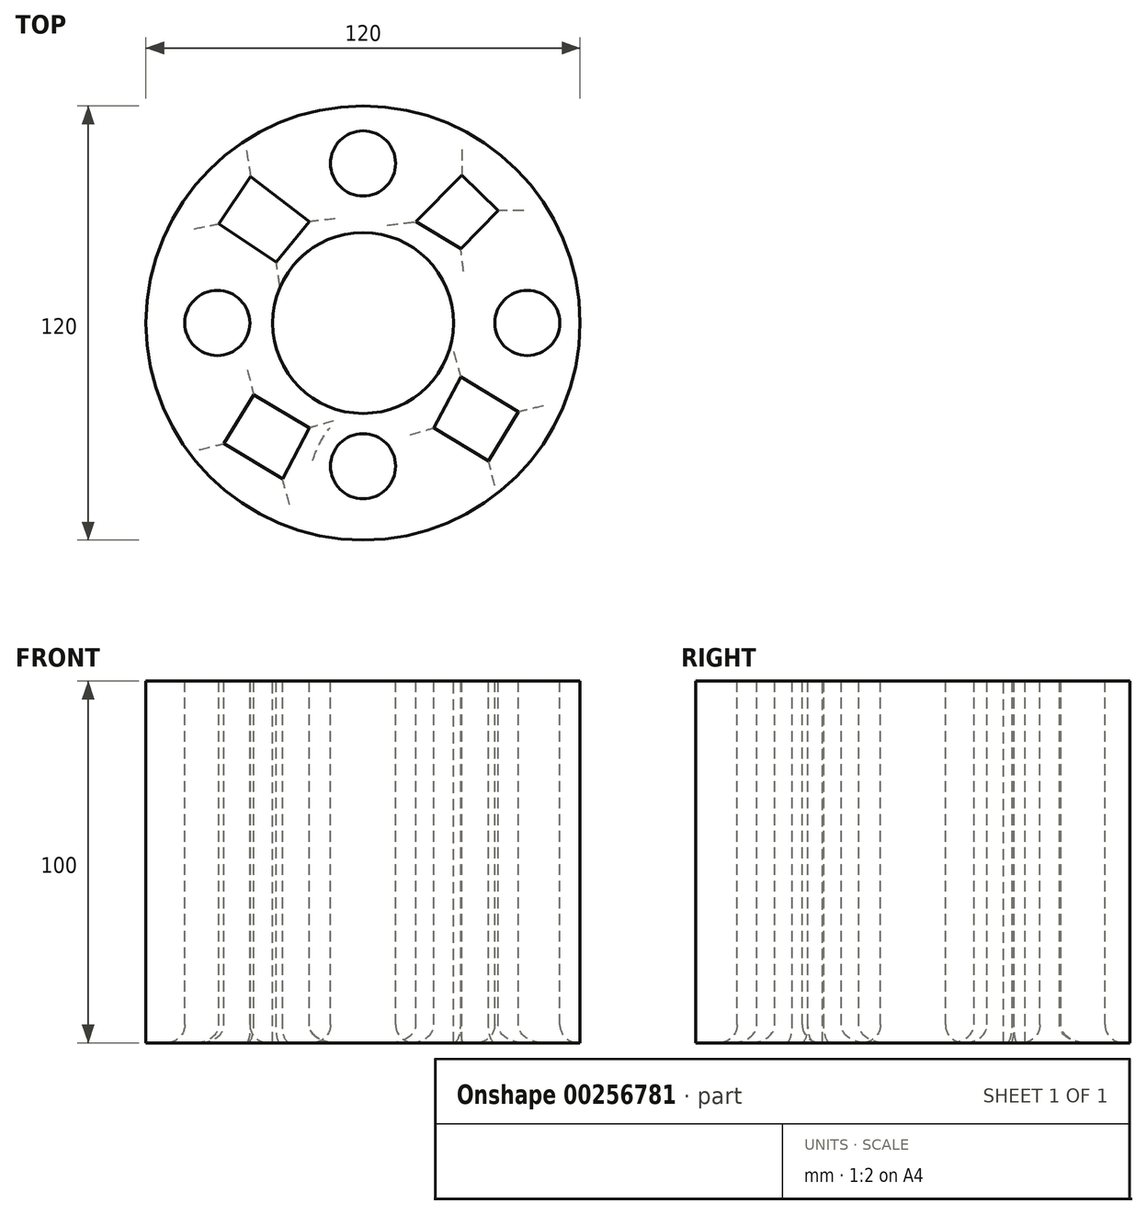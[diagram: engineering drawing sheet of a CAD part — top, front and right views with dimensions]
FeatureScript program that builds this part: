
annotation { "Feature Type Name" : "Feature", "Feature Type Description" : "" }
export const myFeature = defineFeature(function(context is Context, id is Id, definition is map)
    precondition{}
    {
        {
            var Q0;
            Q0=qCreatedBy(makeId("Top.planeOp"),FACE);
            var sketch = newSketch(context, id + "F0", { "sketchPlane" : qUnion([Q0])});
            skCircle(sketch, "E0", {"center": v(0, 0) * mm, "radius": 60 * mm});
            skSolve(sketch);
        }
        {
            var Q0;
            Q0 = qSketchRegion(id + "F0", true);
            extrude(context, id + "F1", {"entities" : qUnion([Q0]), "depth" : 100 * mm});
        }
        {
            var Q0;
            Q0=makeQuery(id+"F1.opExtrude","CAP_FACE",FACE,{"disambiguationData":[OSD([sQuery(id+"F0.wireOp",EDGE,"E0")])],"isStart":false});
            var sketch = newSketch(context, id + "F2", { "sketchPlane" : qUnion([Q0])});
            skCircle(sketch, "E1", {"center": v(0, 0) * mm, "radius": 25 * mm});
            skSolve(sketch);
        }
        {
            var Q0;
            Q0 = qSketchRegion(id + "F2", true);
            extrude(context, id + "F3", {"entities" : qUnion([Q0]), "operationType" : NewBodyOperationType.REMOVE, "endBound" : BoundingType.THROUGH_ALL, "oppositeDirection" : true, "depth" : 25 * mm});
        }
        {
            var Q0;
            Q0=makeQuery(id+"F1.opExtrude","CAP_FACE",FACE,{"disambiguationData":[OSD([sQuery(id+"F0.wireOp",EDGE,"E0")])],"isStart":false});
            var sketch = newSketch(context, id + "F4", { "sketchPlane" : qUnion([Q0])});
            skCircle(sketch, "E2", {"center": v(0, 44.11) * mm, "radius": 9 * mm});
            skCircle(sketch, "E3", {"center": v(-40.28, 0) * mm, "radius": 9 * mm});
            skCircle(sketch, "E4", {"center": v(45.39, 0) * mm, "radius": 9 * mm});
            skCircle(sketch, "E5", {"center": v(0, -39.6) * mm, "radius": 9 * mm});
            skSolve(sketch);
        }
        {
            var Q0;
            Q0 = qSketchRegion(id + "F4", true);
            extrude(context, id + "F5", {"entities" : qUnion([Q0]), "operationType" : NewBodyOperationType.REMOVE, "endBound" : BoundingType.THROUGH_ALL, "oppositeDirection" : true, "depth" : 25 * mm});
        }
        {
            var Q0;
            Q0=makeQuery(id+"F1.opExtrude","CAP_FACE",FACE,{"disambiguationData":[OSD([sQuery(id+"F0.wireOp",EDGE,"E0")])],"isStart":false});
            var sketch = newSketch(context, id + "F6", { "sketchPlane" : qUnion([Q0])});
            skLineSegment(sketch, "E6", {"start": v(-14.83, 28) * mm, "end": v(-24, 16.88) * mm});
            skLineSegment(sketch, "E7", {"start": v(-24, 16.88) * mm, "end": v(-39.81, 27.42) * mm});
            skLineSegment(sketch, "E8", {"start": v(-39.81, 27.42) * mm, "end": v(-31.08, 40.53) * mm});
            skLineSegment(sketch, "E9", {"start": v(-31.08, 40.53) * mm, "end": v(-14.83, 28) * mm});
            skLineSegment(sketch, "E10", {"start": v(14.64, 28) * mm, "end": v(27.32, 40.89) * mm});
            skLineSegment(sketch, "E11", {"start": v(27.32, 40.89) * mm, "end": v(37.35, 31.01) * mm});
            skLineSegment(sketch, "E12", {"start": v(37.35, 31.01) * mm, "end": v(27, 20.51) * mm});
            skLineSegment(sketch, "E13", {"start": v(27, 20.51) * mm, "end": v(14.64, 28) * mm});
            skLineSegment(sketch, "E14", {"start": v(27, -14.93) * mm, "end": v(42.95, -24.6) * mm});
            skLineSegment(sketch, "E15", {"start": v(42.95, -24.6) * mm, "end": v(34.72, -38.18) * mm});
            skLineSegment(sketch, "E16", {"start": v(34.72, -38.18) * mm, "end": v(19.58, -29) * mm});
            skLineSegment(sketch, "E17", {"start": v(19.58, -29) * mm, "end": v(27, -14.93) * mm});
            skLineSegment(sketch, "E18", {"start": v(-14.83, -29) * mm, "end": v(-22.28, -43.12) * mm});
            skLineSegment(sketch, "E19", {"start": v(-22.28, -43.12) * mm, "end": v(-38.42, -33.34) * mm});
            skLineSegment(sketch, "E20", {"start": v(-38.42, -33.34) * mm, "end": v(-30.24, -19.85) * mm});
            skLineSegment(sketch, "E21", {"start": v(-30.24, -19.85) * mm, "end": v(-14.83, -29) * mm});
            skSolve(sketch);
        }
        {
            var Q0;
            Q0 = qSketchRegion(id + "F6", true);
            extrude(context, id + "F7", {"entities" : qUnion([Q0]), "operationType" : NewBodyOperationType.REMOVE, "endBound" : BoundingType.THROUGH_ALL, "oppositeDirection" : true, "depth" : 25 * mm});
        }
        {
            var Q0;
            Q0=makeQuery(id+"F7.boolean.opBoolean","COPY",EDGE,{"derivedFrom":makeQuery(id+"F7.opExtrude","CAP_EDGE",EDGE,{"disambiguationData":[OSD([sQuery(id+"F6.wireOp",EDGE,"E13")])],"isStart":true})});
            var Q1;
            Q1=makeQuery(id+"F7.boolean.opBoolean","INTERSECT",EDGE,{"derivedFrom":[makeQuery(id+"F1.opExtrude","CAP_FACE",FACE,{"disambiguationData":[OSD([sQuery(id+"F0.wireOp",EDGE,"E0")])],"isStart":true}),makeQuery(id+"F7.opExtrude","SWEPT_FACE",FACE,{"disambiguationData":[OSD([sQuery(id+"F6.wireOp",EDGE,"E13")])]})]});
            var Q2;
            Q2=makeQuery(id+"F7.boolean.opBoolean","INTERSECT",EDGE,{"derivedFrom":[makeQuery(id+"F1.opExtrude","CAP_FACE",FACE,{"disambiguationData":[OSD([sQuery(id+"F0.wireOp",EDGE,"E0")])],"isStart":true}),makeQuery(id+"F7.opExtrude","SWEPT_FACE",FACE,{"disambiguationData":[OSD([sQuery(id+"F6.wireOp",EDGE,"E10")])]})]});
            var Q3;
            Q3=makeQuery(id+"F7.boolean.opBoolean","INTERSECT",EDGE,{"derivedFrom":[makeQuery(id+"F1.opExtrude","CAP_FACE",FACE,{"disambiguationData":[OSD([sQuery(id+"F0.wireOp",EDGE,"E0")])],"isStart":true}),makeQuery(id+"F7.opExtrude","SWEPT_FACE",FACE,{"disambiguationData":[OSD([sQuery(id+"F6.wireOp",EDGE,"E12")])]})]});
            var Q4;
            Q4=makeQuery(id+"F7.boolean.opBoolean","INTERSECT",EDGE,{"derivedFrom":[makeQuery(id+"F1.opExtrude","CAP_FACE",FACE,{"disambiguationData":[OSD([sQuery(id+"F0.wireOp",EDGE,"E0")])],"isStart":true}),makeQuery(id+"F7.opExtrude","SWEPT_FACE",FACE,{"disambiguationData":[OSD([sQuery(id+"F6.wireOp",EDGE,"E11")])]})]});
            var Q5;
            Q5=makeQuery(id+"F7.boolean.opBoolean","COPY",EDGE,{"derivedFrom":makeQuery(id+"F7.opExtrude","CAP_EDGE",EDGE,{"disambiguationData":[OSD([sQuery(id+"F6.wireOp",EDGE,"E10")])],"isStart":true})});
            var Q6;
            Q6=makeQuery(id+"F7.boolean.opBoolean","COPY",EDGE,{"derivedFrom":makeQuery(id+"F7.opExtrude","CAP_EDGE",EDGE,{"disambiguationData":[OSD([sQuery(id+"F6.wireOp",EDGE,"E11")])],"isStart":true})});
            var Q7;
            Q7=makeQuery(id+"F7.boolean.opBoolean","COPY",EDGE,{"derivedFrom":makeQuery(id+"F7.opExtrude","CAP_EDGE",EDGE,{"disambiguationData":[OSD([sQuery(id+"F6.wireOp",EDGE,"E12")])],"isStart":true})});
            var Q8;
            Q8=makeQuery(id+"F7.boolean.opBoolean","COPY",EDGE,{"derivedFrom":makeQuery(id+"F7.opExtrude","CAP_EDGE",EDGE,{"disambiguationData":[OSD([sQuery(id+"F6.wireOp",EDGE,"E9")])],"isStart":true})});
            var Q9;
            Q9=makeQuery(id+"F7.boolean.opBoolean","COPY",EDGE,{"derivedFrom":makeQuery(id+"F7.opExtrude","CAP_EDGE",EDGE,{"disambiguationData":[OSD([sQuery(id+"F6.wireOp",EDGE,"E8")])],"isStart":true})});
            var Q10;
            Q10=makeQuery(id+"F7.boolean.opBoolean","COPY",EDGE,{"derivedFrom":makeQuery(id+"F7.opExtrude","CAP_EDGE",EDGE,{"disambiguationData":[OSD([sQuery(id+"F6.wireOp",EDGE,"E7")])],"isStart":true})});
            var Q11;
            Q11=makeQuery(id+"F7.boolean.opBoolean","COPY",EDGE,{"derivedFrom":makeQuery(id+"F7.opExtrude","CAP_EDGE",EDGE,{"disambiguationData":[OSD([sQuery(id+"F6.wireOp",EDGE,"E6")])],"isStart":true})});
            var Q12;
            Q12=makeQuery(id+"F7.boolean.opBoolean","COPY",EDGE,{"derivedFrom":makeQuery(id+"F7.opExtrude","CAP_EDGE",EDGE,{"disambiguationData":[OSD([sQuery(id+"F6.wireOp",EDGE,"E21")])],"isStart":true})});
            var Q13;
            Q13=makeQuery(id+"F7.boolean.opBoolean","COPY",EDGE,{"derivedFrom":makeQuery(id+"F7.opExtrude","CAP_EDGE",EDGE,{"disambiguationData":[OSD([sQuery(id+"F6.wireOp",EDGE,"E20")])],"isStart":true})});
            var Q14;
            Q14=makeQuery(id+"F7.boolean.opBoolean","COPY",EDGE,{"derivedFrom":makeQuery(id+"F7.opExtrude","CAP_EDGE",EDGE,{"disambiguationData":[OSD([sQuery(id+"F6.wireOp",EDGE,"E19")])],"isStart":true})});
            var Q15;
            Q15=makeQuery(id+"F7.boolean.opBoolean","COPY",EDGE,{"derivedFrom":makeQuery(id+"F7.opExtrude","CAP_EDGE",EDGE,{"disambiguationData":[OSD([sQuery(id+"F6.wireOp",EDGE,"E18")])],"isStart":true})});
            var Q16;
            Q16=makeQuery(id+"F7.boolean.opBoolean","COPY",EDGE,{"derivedFrom":makeQuery(id+"F7.opExtrude","CAP_EDGE",EDGE,{"disambiguationData":[OSD([sQuery(id+"F6.wireOp",EDGE,"E16")])],"isStart":true})});
            var Q17;
            Q17=makeQuery(id+"F7.boolean.opBoolean","COPY",EDGE,{"derivedFrom":makeQuery(id+"F7.opExtrude","CAP_EDGE",EDGE,{"disambiguationData":[OSD([sQuery(id+"F6.wireOp",EDGE,"E17")])],"isStart":true})});
            var Q18;
            Q18=makeQuery(id+"F7.boolean.opBoolean","COPY",EDGE,{"derivedFrom":makeQuery(id+"F7.opExtrude","CAP_EDGE",EDGE,{"disambiguationData":[OSD([sQuery(id+"F6.wireOp",EDGE,"E14")])],"isStart":true})});
            var Q19;
            Q19=makeQuery(id+"F7.boolean.opBoolean","COPY",EDGE,{"derivedFrom":makeQuery(id+"F7.opExtrude","CAP_EDGE",EDGE,{"disambiguationData":[OSD([sQuery(id+"F6.wireOp",EDGE,"E15")])],"isStart":true})});
            var Q20;
            Q20=makeQuery(id+"F5.boolean.opBoolean","COPY",EDGE,{"derivedFrom":makeQuery(id+"F5.opExtrude","CAP_EDGE",EDGE,{"disambiguationData":[OSD([sQuery(id+"F4.wireOp",EDGE,"E4")])],"isStart":true})});
            var Q21;
            Q21=makeQuery(id+"F5.boolean.opBoolean","COPY",EDGE,{"derivedFrom":makeQuery(id+"F5.opExtrude","CAP_EDGE",EDGE,{"disambiguationData":[OSD([sQuery(id+"F4.wireOp",EDGE,"E2")])],"isStart":true})});
            var Q22;
            Q22=makeQuery(id+"F5.boolean.opBoolean","COPY",EDGE,{"derivedFrom":makeQuery(id+"F5.opExtrude","CAP_EDGE",EDGE,{"disambiguationData":[OSD([sQuery(id+"F4.wireOp",EDGE,"E3")])],"isStart":true})});
            var Q23;
            Q23=makeQuery(id+"F5.boolean.opBoolean","COPY",EDGE,{"derivedFrom":makeQuery(id+"F5.opExtrude","CAP_EDGE",EDGE,{"disambiguationData":[OSD([sQuery(id+"F4.wireOp",EDGE,"E5")])],"isStart":true})});
            var Q24;
            Q24=makeQuery(id+"F7.boolean.opBoolean","INTERSECT",EDGE,{"derivedFrom":[makeQuery(id+"F1.opExtrude","CAP_FACE",FACE,{"disambiguationData":[OSD([sQuery(id+"F0.wireOp",EDGE,"E0")])],"isStart":true}),makeQuery(id+"F7.opExtrude","SWEPT_FACE",FACE,{"disambiguationData":[OSD([sQuery(id+"F6.wireOp",EDGE,"E14")])]})]});
            var Q25;
            Q25=makeQuery(id+"F7.boolean.opBoolean","INTERSECT",EDGE,{"derivedFrom":[makeQuery(id+"F1.opExtrude","CAP_FACE",FACE,{"disambiguationData":[OSD([sQuery(id+"F0.wireOp",EDGE,"E0")])],"isStart":true}),makeQuery(id+"F7.opExtrude","SWEPT_FACE",FACE,{"disambiguationData":[OSD([sQuery(id+"F6.wireOp",EDGE,"E17")])]})]});
            var Q26;
            Q26=makeQuery(id+"F7.boolean.opBoolean","INTERSECT",EDGE,{"derivedFrom":[makeQuery(id+"F1.opExtrude","CAP_FACE",FACE,{"disambiguationData":[OSD([sQuery(id+"F0.wireOp",EDGE,"E0")])],"isStart":true}),makeQuery(id+"F7.opExtrude","SWEPT_FACE",FACE,{"disambiguationData":[OSD([sQuery(id+"F6.wireOp",EDGE,"E16")])]})]});
            var Q27;
            Q27=makeQuery(id+"F7.boolean.opBoolean","INTERSECT",EDGE,{"derivedFrom":[makeQuery(id+"F1.opExtrude","CAP_FACE",FACE,{"disambiguationData":[OSD([sQuery(id+"F0.wireOp",EDGE,"E0")])],"isStart":true}),makeQuery(id+"F7.opExtrude","SWEPT_FACE",FACE,{"disambiguationData":[OSD([sQuery(id+"F6.wireOp",EDGE,"E15")])]})]});
            var Q28;
            Q28=makeQuery(id+"F5.boolean.opBoolean","INTERSECT",EDGE,{"derivedFrom":[makeQuery(id+"F1.opExtrude","CAP_FACE",FACE,{"disambiguationData":[OSD([sQuery(id+"F0.wireOp",EDGE,"E0")])],"isStart":true}),makeQuery(id+"F5.opExtrude","SWEPT_FACE",FACE,{"disambiguationData":[OSD([sQuery(id+"F4.wireOp",EDGE,"E4")])]})]});
            var Q29;
            Q29=makeQuery(id+"F5.boolean.opBoolean","INTERSECT",EDGE,{"derivedFrom":[makeQuery(id+"F1.opExtrude","CAP_FACE",FACE,{"disambiguationData":[OSD([sQuery(id+"F0.wireOp",EDGE,"E0")])],"isStart":true}),makeQuery(id+"F5.opExtrude","SWEPT_FACE",FACE,{"disambiguationData":[OSD([sQuery(id+"F4.wireOp",EDGE,"E2")])]})]});
            var Q30;
            Q30=makeQuery(id+"F7.boolean.opBoolean","INTERSECT",EDGE,{"derivedFrom":[makeQuery(id+"F1.opExtrude","CAP_FACE",FACE,{"disambiguationData":[OSD([sQuery(id+"F0.wireOp",EDGE,"E0")])],"isStart":true}),makeQuery(id+"F7.opExtrude","SWEPT_FACE",FACE,{"disambiguationData":[OSD([sQuery(id+"F6.wireOp",EDGE,"E9")])]})]});
            var Q31;
            Q31=makeQuery(id+"F7.boolean.opBoolean","INTERSECT",EDGE,{"derivedFrom":[makeQuery(id+"F1.opExtrude","CAP_FACE",FACE,{"disambiguationData":[OSD([sQuery(id+"F0.wireOp",EDGE,"E0")])],"isStart":true}),makeQuery(id+"F7.opExtrude","SWEPT_FACE",FACE,{"disambiguationData":[OSD([sQuery(id+"F6.wireOp",EDGE,"E8")])]})]});
            var Q32;
            Q32=makeQuery(id+"F7.boolean.opBoolean","INTERSECT",EDGE,{"derivedFrom":[makeQuery(id+"F1.opExtrude","CAP_FACE",FACE,{"disambiguationData":[OSD([sQuery(id+"F0.wireOp",EDGE,"E0")])],"isStart":true}),makeQuery(id+"F7.opExtrude","SWEPT_FACE",FACE,{"disambiguationData":[OSD([sQuery(id+"F6.wireOp",EDGE,"E6")])]})]});
            var Q33;
            Q33=makeQuery(id+"F7.boolean.opBoolean","INTERSECT",EDGE,{"derivedFrom":[makeQuery(id+"F1.opExtrude","CAP_FACE",FACE,{"disambiguationData":[OSD([sQuery(id+"F0.wireOp",EDGE,"E0")])],"isStart":true}),makeQuery(id+"F7.opExtrude","SWEPT_FACE",FACE,{"disambiguationData":[OSD([sQuery(id+"F6.wireOp",EDGE,"E7")])]})]});
            var Q34;
            Q34=makeQuery(id+"F5.boolean.opBoolean","INTERSECT",EDGE,{"derivedFrom":[makeQuery(id+"F1.opExtrude","CAP_FACE",FACE,{"disambiguationData":[OSD([sQuery(id+"F0.wireOp",EDGE,"E0")])],"isStart":true}),makeQuery(id+"F5.opExtrude","SWEPT_FACE",FACE,{"disambiguationData":[OSD([sQuery(id+"F4.wireOp",EDGE,"E3")])]})]});
            var Q35;
            Q35=makeQuery(id+"F7.boolean.opBoolean","INTERSECT",EDGE,{"derivedFrom":[makeQuery(id+"F1.opExtrude","CAP_FACE",FACE,{"disambiguationData":[OSD([sQuery(id+"F0.wireOp",EDGE,"E0")])],"isStart":true}),makeQuery(id+"F7.opExtrude","SWEPT_FACE",FACE,{"disambiguationData":[OSD([sQuery(id+"F6.wireOp",EDGE,"E21")])]})]});
            var Q36;
            Q36=makeQuery(id+"F7.boolean.opBoolean","INTERSECT",EDGE,{"derivedFrom":[makeQuery(id+"F1.opExtrude","CAP_FACE",FACE,{"disambiguationData":[OSD([sQuery(id+"F0.wireOp",EDGE,"E0")])],"isStart":true}),makeQuery(id+"F7.opExtrude","SWEPT_FACE",FACE,{"disambiguationData":[OSD([sQuery(id+"F6.wireOp",EDGE,"E20")])]})]});
            var Q37;
            Q37=makeQuery(id+"F7.boolean.opBoolean","INTERSECT",EDGE,{"derivedFrom":[makeQuery(id+"F1.opExtrude","CAP_FACE",FACE,{"disambiguationData":[OSD([sQuery(id+"F0.wireOp",EDGE,"E0")])],"isStart":true}),makeQuery(id+"F7.opExtrude","SWEPT_FACE",FACE,{"disambiguationData":[OSD([sQuery(id+"F6.wireOp",EDGE,"E19")])]})]});
            var Q38;
            Q38=makeQuery(id+"F7.boolean.opBoolean","INTERSECT",EDGE,{"derivedFrom":[makeQuery(id+"F1.opExtrude","CAP_FACE",FACE,{"disambiguationData":[OSD([sQuery(id+"F0.wireOp",EDGE,"E0")])],"isStart":true}),makeQuery(id+"F7.opExtrude","SWEPT_FACE",FACE,{"disambiguationData":[OSD([sQuery(id+"F6.wireOp",EDGE,"E18")])]})]});
            var Q39;
            Q39=makeQuery(id+"F5.boolean.opBoolean","INTERSECT",EDGE,{"derivedFrom":[makeQuery(id+"F1.opExtrude","CAP_FACE",FACE,{"disambiguationData":[OSD([sQuery(id+"F0.wireOp",EDGE,"E0")])],"isStart":true}),makeQuery(id+"F5.opExtrude","SWEPT_FACE",FACE,{"disambiguationData":[OSD([sQuery(id+"F4.wireOp",EDGE,"E5")])]})]});
            fillet(context, id + "F8", {"entities" : qUnion([Q0, Q1, Q2, Q3, Q4, Q5, Q6, Q7, Q8, Q9, Q10, Q11, Q12, Q13, Q14, Q15, Q16, Q17, Q18, Q19, Q20, Q21, Q22, Q23, Q24, Q25, Q26, Q27, Q28, Q29, Q30, Q31, Q32, Q33, Q34, Q35, Q36, Q37, Q38, Q39]), "radius" : 5 * mm, "tangentPropagation" : true, "allowEdgeOverflow" : false});
        }
    });
